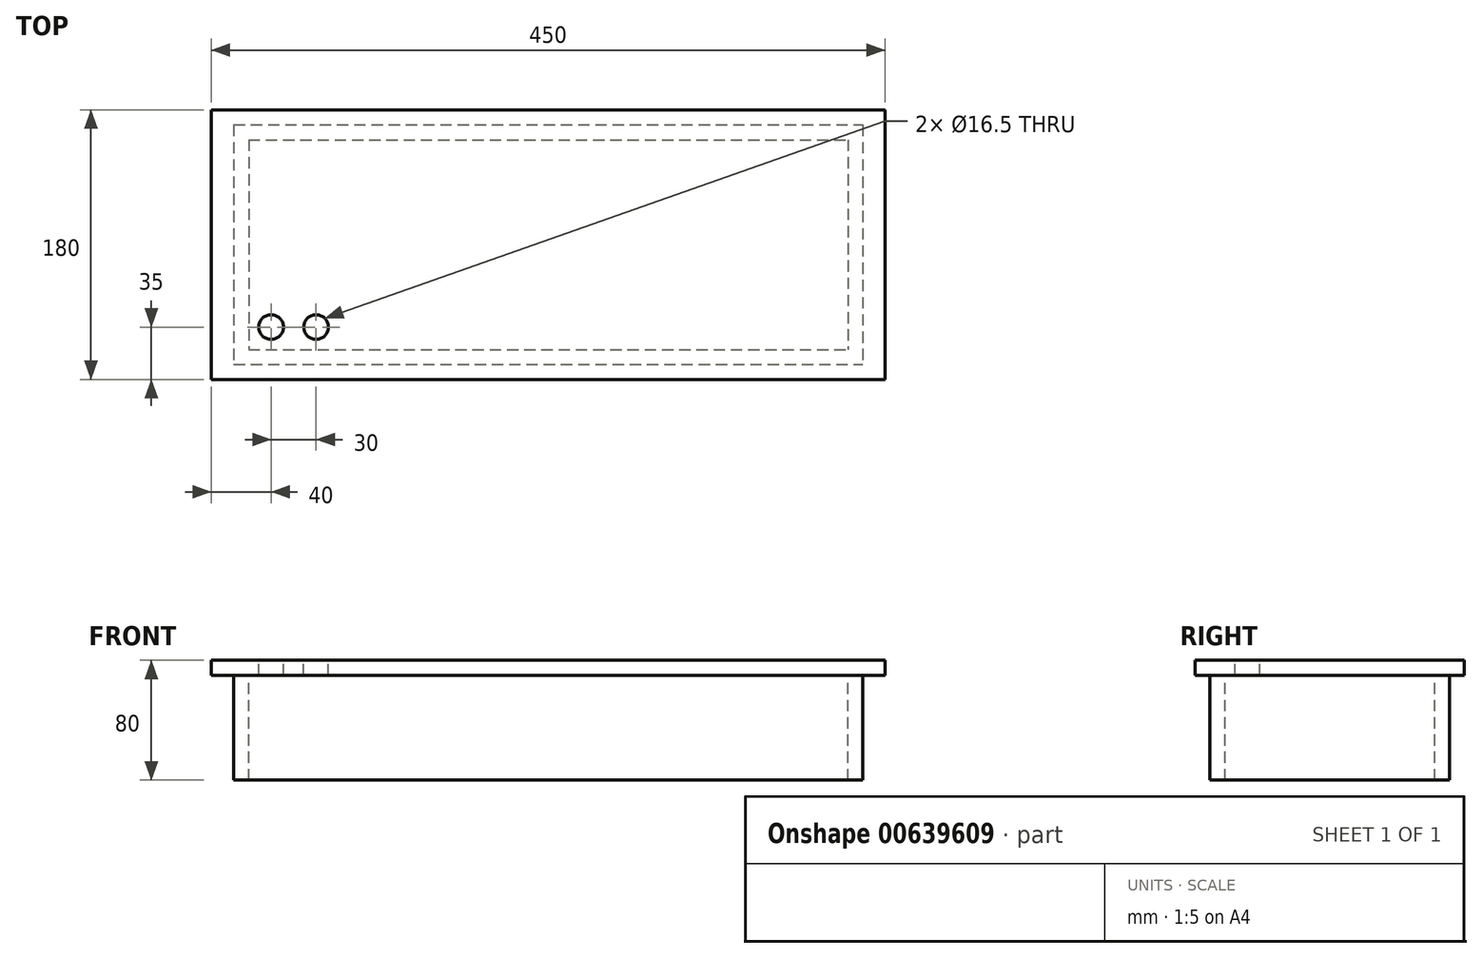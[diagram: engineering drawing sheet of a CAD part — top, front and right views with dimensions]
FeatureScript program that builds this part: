
annotation { "Feature Type Name" : "Feature", "Feature Type Description" : "" }
export const myFeature = defineFeature(function(context is Context, id is Id, definition is map)
    precondition{}
    {
        {
            var Q0;
            Q0=qCreatedBy(makeId("Top.planeOp"),FACE);
            var sketch = newSketch(context, id + "F0", { "sketchPlane" : qUnion([Q0])});
            skLineSegment(sketch, "E0.bottom", {"start": v(225, -90) * mm, "end": v(-225, -90) * mm});
            skLineSegment(sketch, "E0.top", {"start": v(225, 90) * mm, "end": v(-225, 90) * mm});
            skLineSegment(sketch, "E0.left", {"start": v(225, -90) * mm, "end": v(225, 90) * mm});
            skLineSegment(sketch, "E0.right", {"start": v(-225, -90) * mm, "end": v(-225, 90) * mm});
            skPoint(sketch, "E0.middle", {"position": v(0, 0) * mm});
            skSolve(sketch);
        }
        {
            var Q0;
            Q0 = qSketchRegion(id + "F0", true);
            extrude(context, id + "F1", {"entities" : qUnion([Q0]), "depth" : 10 * mm, "offsetDistance" : 25 * mm});
        }
        {
            var Q0;
            Q0=makeQuery(id+"F1.opExtrude","CAP_FACE",FACE,{"disambiguationData":[OSD([sQuery(id+"F0.wireOp",EDGE,"E0.bottom"),sQuery(id+"F0.wireOp",EDGE,"E0.top"),sQuery(id+"F0.wireOp",EDGE,"E0.left"),sQuery(id+"F0.wireOp",EDGE,"E0.right")])],"isStart":true});
            var sketch = newSketch(context, id + "F2", { "sketchPlane" : qUnion([Q0])});
            skLineSegment(sketch, "E1.bottom", {"start": v(-210, -80) * mm, "end": v(210, -80) * mm});
            skLineSegment(sketch, "E1.top", {"start": v(-210, 80) * mm, "end": v(210, 80) * mm});
            skLineSegment(sketch, "E1.left", {"start": v(-210, -80) * mm, "end": v(-210, 80) * mm});
            skLineSegment(sketch, "E1.right", {"start": v(210, -80) * mm, "end": v(210, 80) * mm});
            skPoint(sketch, "E1.middle", {"position": v(0, 0) * mm});
            skLineSegment(sketch, "E2.bottom", {"start": v(-200, -70) * mm, "end": v(200, -70) * mm});
            skLineSegment(sketch, "E2.top", {"start": v(-200, 70) * mm, "end": v(200, 70) * mm});
            skLineSegment(sketch, "E2.left", {"start": v(-200, -70) * mm, "end": v(-200, 70) * mm});
            skLineSegment(sketch, "E2.right", {"start": v(200, -70) * mm, "end": v(200, 70) * mm});
            skSolve(sketch);
        }
        {
            var Q0;
            Q0=makeQuery(id+"F2.imprint","IMPRINT",FACE,{"disambiguationData":[TD([[makeQuery(id+"F2.imprint","IMPRINT",EDGE,{"derivedFrom":sQuery(id+"F2.wireOp",EDGE,"E1.bottom")}),1.0]])]});
            extrude(context, id + "F3", {"entities" : qUnion([Q0]), "operationType" : NewBodyOperationType.ADD, "depth" : 70 * mm, "offsetDistance" : 25 * mm});
        }
        {
            var Q0;
            Q0=makeQuery(id+"F1.opExtrude","CAP_FACE",FACE,{"disambiguationData":[OSD([sQuery(id+"F0.wireOp",EDGE,"E0.bottom"),sQuery(id+"F0.wireOp",EDGE,"E0.top"),sQuery(id+"F0.wireOp",EDGE,"E0.left"),sQuery(id+"F0.wireOp",EDGE,"E0.right")])],"isStart":false});
            var sketch = newSketch(context, id + "F4", { "sketchPlane" : qUnion([Q0])});
            skPoint(sketch, "E3", {"position": v(-185, -55) * mm});
            skPoint(sketch, "E4", {"position": v(-155, -55) * mm});
            skSolve(sketch);
        }
        {
            var Q0;
            Q0=sQuery(id+"F4.wireOp",VERTEX,"E3");
            var Q1;
            Q1=sQuery(id+"F4.wireOp",VERTEX,"E4");
            var Q2;
            Q2=makeQuery(id+"F1.opExtrude","SWEPT_BODY",BODY,{"disambiguationData":[OSD([sQuery(id+"F0.wireOp",EDGE,"E0.bottom"),sQuery(id+"F0.wireOp",EDGE,"E0.top"),sQuery(id+"F0.wireOp",EDGE,"E0.left"),sQuery(id+"F0.wireOp",EDGE,"E0.right")])]});
            hole(context, id + "F5", {"style" : HoleStyle.SIMPLE, "endStyle" : HoleEndStyle.THROUGH, "holeDiameter" : 16.5 * mm, "majorDiameter" : 5 * mm, "isTappedThrough" : true, "tappedDepth" : 12 * mm, "tapClearance" : 3, "locations" : qUnion([Q0, Q1]), "scope" : qUnion([Q2])});
        }
    });
